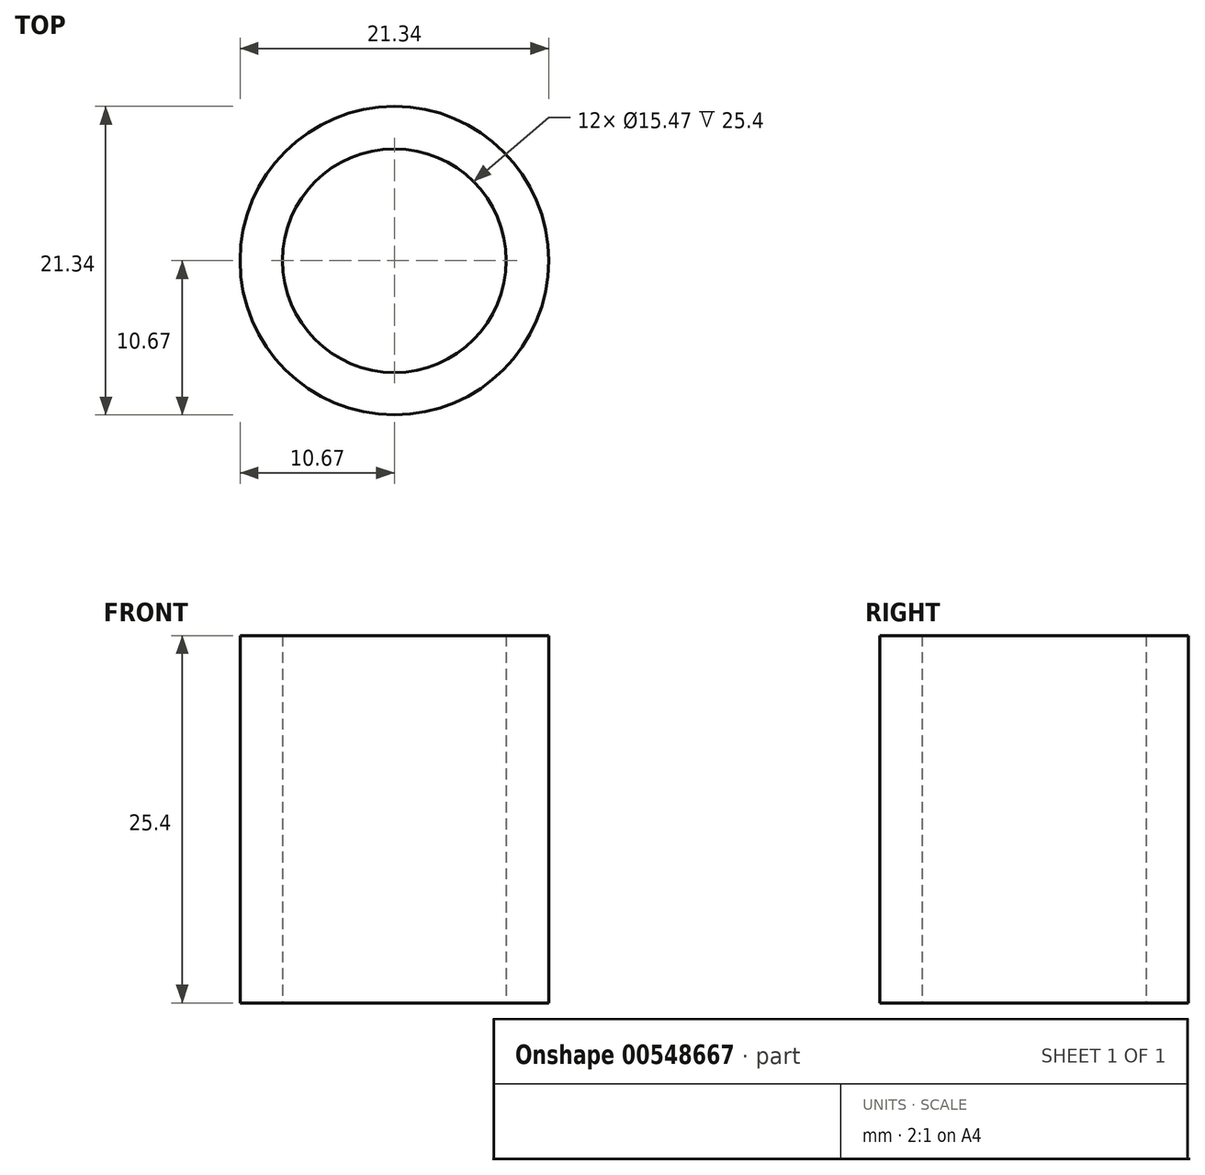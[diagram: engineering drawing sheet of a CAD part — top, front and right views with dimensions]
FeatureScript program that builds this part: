
annotation { "Feature Type Name" : "Feature", "Feature Type Description" : "" }
export const myFeature = defineFeature(function(context is Context, id is Id, definition is map)
    precondition{}
    {
        {
            var Q0;
            Q0=qCreatedBy(makeId("Top.planeOp"),FACE);
            var sketch = newSketch(context, id + "F0", { "sketchPlane" : qUnion([Q0])});
            skCircle(sketch, "E0", {"center": v(0, 0) * mm, "radius": 7.73 * mm});
            skCircle(sketch, "E1", {"center": v(0, 0) * mm, "radius": 10.67 * mm});
            skSolve(sketch);
        }
        {
            var Q0;
            Q0=makeQuery(id+"F0.imprint","IMPRINT",FACE,{"disambiguationData":[TD([[makeQuery(id+"F0.imprint","IMPRINT",EDGE,{"derivedFrom":sQuery(id+"F0.wireOp",EDGE,"E0")}),-1.0]])]});
            extrude(context, id + "F1", {"entities" : qUnion([Q0]), "endBound" : BoundingType.SYMMETRIC, "depth" : 25.4 * mm, "offsetDistance" : 25.4 * mm});
        }
    });
